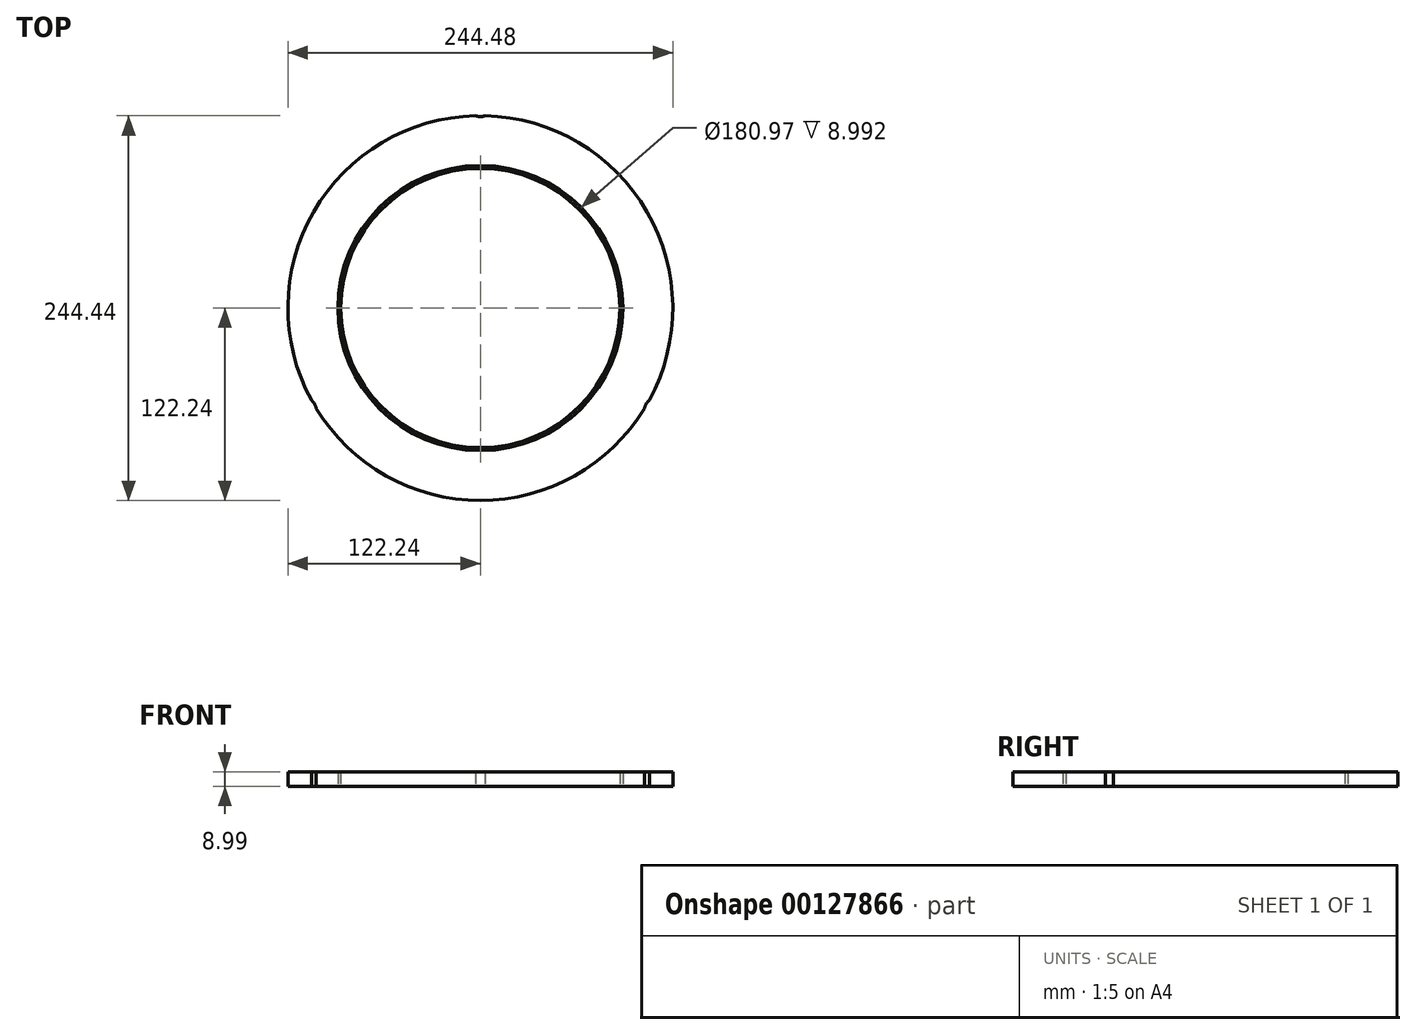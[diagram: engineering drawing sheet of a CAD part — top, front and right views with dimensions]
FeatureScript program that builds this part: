
annotation { "Feature Type Name" : "Feature", "Feature Type Description" : "" }
export const myFeature = defineFeature(function(context is Context, id is Id, definition is map)
    precondition{}
    {
        {
            var Q0;
            Q0=qCreatedBy(makeId("Top.planeOp"),FACE);
            var sketch = newSketch(context, id + "F3", { "sketchPlane" : qUnion([Q0])});
            skCircle(sketch, "E0", {"center": v(0, 0) * mm, "radius": 88.65 * mm});
            skSolve(sketch);
        }
        {
            var Q0;
            Q0 = qSketchRegion(id + "F3", true);
            extrude(context, id + "F0", {"entities" : qUnion([Q0]), "depth" : 9 * mm});
        }
        {
            var Q0;
            Q0=qCreatedBy(makeId("Top.planeOp"),FACE);
            var sketch = newSketch(context, id + "F1", { "sketchPlane" : qUnion([Q0])});
            skCircle(sketch, "E1", {"center": v(0, 0) * mm, "radius": 90.49 * mm});
            skCircle(sketch, "E2", {"center": v(0, 0) * mm, "radius": 122.24 * mm});
            skCircle(sketch, "E3", {"center": v(0, 129.24) * mm, "radius": 7.64 * mm});
            skCircle(sketch, "E4", {"center": v(0, 129.24) * mm, "radius": 3.83 * mm});
            skCircle(sketch, "E5.1.0", {"center": v(-111.92, -64.62) * mm, "radius": 3.83 * mm});
            skCircle(sketch, "E5.1.1", {"center": v(-111.92, -64.62) * mm, "radius": 7.64 * mm});
            skCircle(sketch, "E5.2.0", {"center": v(111.92, -64.62) * mm, "radius": 3.83 * mm});
            skCircle(sketch, "E5.2.1", {"center": v(111.92, -64.62) * mm, "radius": 7.64 * mm});
            skSolve(sketch);
        }
        {
            var Q0;
            Q0=makeQuery(id+"F1.imprint","IMPRINT",FACE,{"disambiguationData":[TD([[makeQuery(id+"F1.imprint","IMPRINT",EDGE,{"derivedFrom":sQuery(id+"F1.wireOp",EDGE,"E1")}),-1.0]])]});
            extrude(context, id + "F2", {"entities" : qUnion([Q0]), "depth" : 9 * mm});
        }
    });
